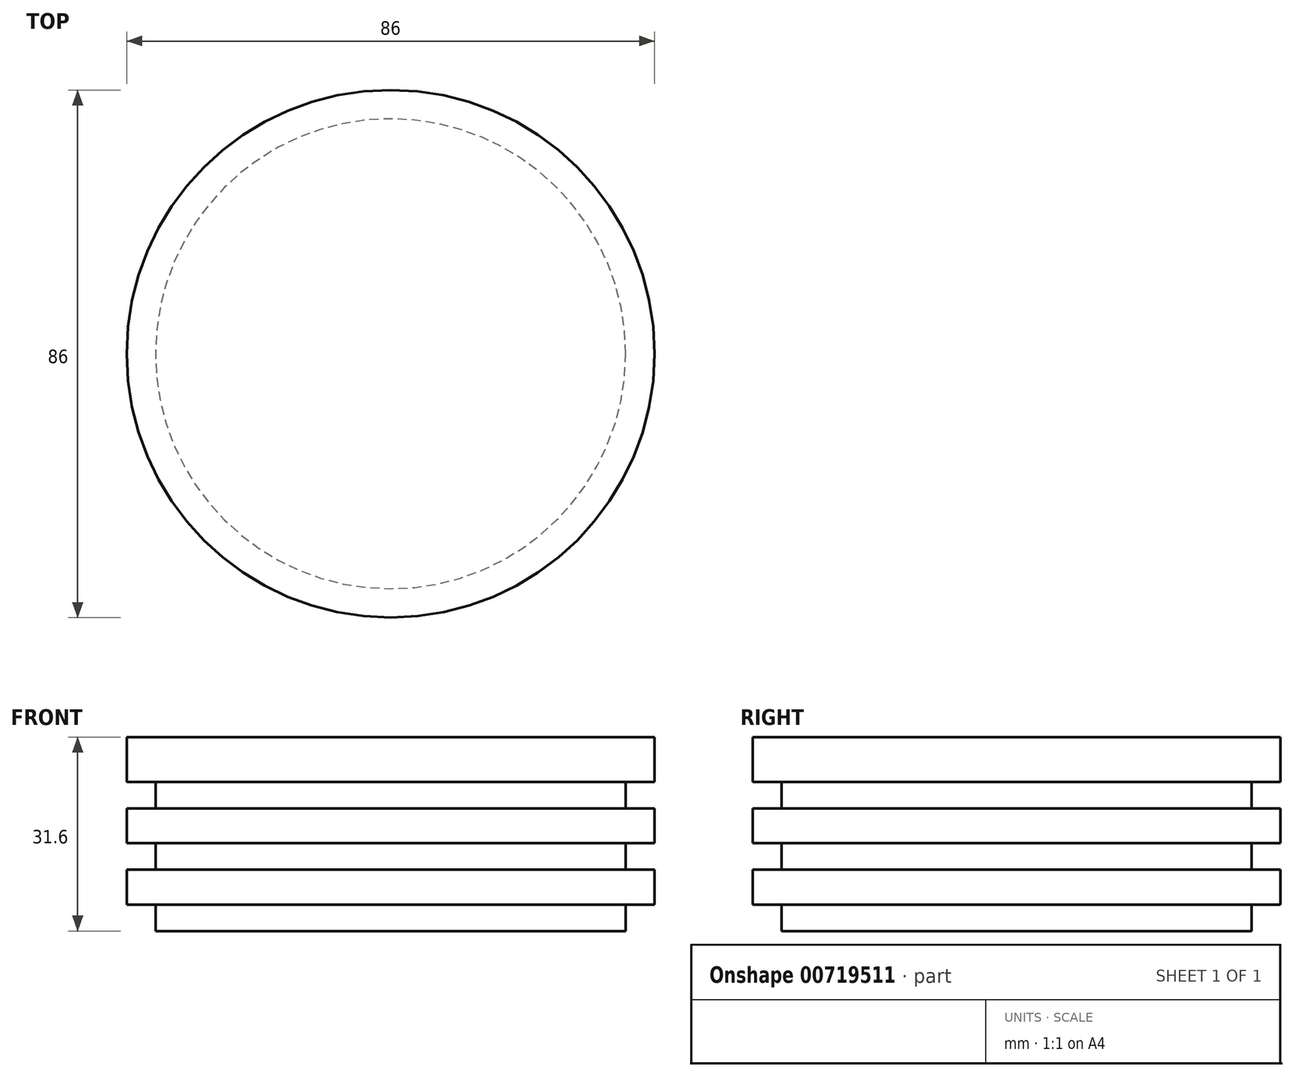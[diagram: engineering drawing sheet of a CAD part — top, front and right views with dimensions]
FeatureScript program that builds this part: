
annotation { "Feature Type Name" : "Feature", "Feature Type Description" : "" }
export const myFeature = defineFeature(function(context is Context, id is Id, definition is map)
    precondition{}
    {
        {
            var Q0;
            Q0=qCreatedBy(makeId("Top.planeOp"),FACE);
            var sketch = newSketch(context, id + "F0", { "sketchPlane" : qUnion([Q0])});
            skCircle(sketch, "E0", {"center": v(0, 0) * mm, "radius": 43 * mm});
            skSolve(sketch);
        }
        {
            var Q0;
            Q0=makeQuery(id+"F0.imprint","IMPRINT",FACE,{"disambiguationData":[TD([[makeQuery(id+"F0.imprint","IMPRINT",EDGE,{"derivedFrom":sQuery(id+"F0.wireOp",EDGE,"E0")}),1.0]])]});
            extrude(context, id + "F1", {"entities" : qUnion([Q0]), "depth" : 7.3 * mm, "offsetDistance" : 25 * mm});
        }
        {
            var Q0;
            Q0=makeQuery(id+"F1.opExtrude","CAP_FACE",FACE,{"disambiguationData":[OSD([sQuery(id+"F0.wireOp",EDGE,"E0")])],"isStart":true});
            var sketch = newSketch(context, id + "F2", { "sketchPlane" : qUnion([Q0])});
            skCircle(sketch, "E1", {"center": v(0, 0) * mm, "radius": 38.3 * mm});
            skSolve(sketch);
        }
        {
            var Q0;
            Q0=makeQuery(id+"F2.imprint","IMPRINT",FACE,{"disambiguationData":[TD([[makeQuery(id+"F2.imprint","IMPRINT",EDGE,{"derivedFrom":sQuery(id+"F2.wireOp",EDGE,"E1")}),1.0]])]});
            extrude(context, id + "F3", {"entities" : qUnion([Q0]), "operationType" : NewBodyOperationType.ADD, "depth" : 4.3 * mm, "offsetDistance" : 25 * mm});
        }
        {
            var Q0;
            Q0=makeQuery(id+"F3.opExtrude","CAP_FACE",FACE,{"disambiguationData":[OSD([sQuery(id+"F2.wireOp",EDGE,"E1")])],"isStart":false});
            var sketch = newSketch(context, id + "F4", { "sketchPlane" : qUnion([Q0])});
            skCircle(sketch, "E2.0", {"center": v(0, 0) * mm, "radius": 43 * mm});
            skSolve(sketch);
        }
        {
            var Q0;
            Q0 = qSketchRegion(id + "F4", true);
            extrude(context, id + "F5", {"entities" : qUnion([Q0]), "operationType" : NewBodyOperationType.ADD, "depth" : 5.7 * mm, "offsetDistance" : 25 * mm});
        }
        {
            var Q0;
            Q0=makeQuery(id+"F5.opExtrude","CAP_FACE",FACE,{"disambiguationData":[OSD([sQuery(id+"F4.wireOp",EDGE,"E2.0")])],"isStart":false});
            var sketch = newSketch(context, id + "F6", { "sketchPlane" : qUnion([Q0])});
            skCircle(sketch, "E3.0", {"center": v(0, 0) * mm, "radius": 38.3 * mm});
            skSolve(sketch);
        }
        {
            var Q0;
            Q0=makeQuery(id+"F6.imprint","IMPRINT",FACE,{"disambiguationData":[TD([[makeQuery(id+"F6.imprint","IMPRINT",EDGE,{"derivedFrom":sQuery(id+"F6.wireOp",EDGE,"E3.0")}),1.0]])]});
            extrude(context, id + "F7", {"entities" : qUnion([Q0]), "operationType" : NewBodyOperationType.ADD, "depth" : 4.3 * mm, "offsetDistance" : 25 * mm});
        }
        {
            var Q0;
            Q0=makeQuery(id+"F7.opExtrude","CAP_FACE",FACE,{"disambiguationData":[OSD([sQuery(id+"F6.wireOp",EDGE,"E3.0")])],"isStart":false});
            var sketch = newSketch(context, id + "F8", { "sketchPlane" : qUnion([Q0])});
            skCircle(sketch, "E4.0", {"center": v(0, 0) * mm, "radius": 43 * mm});
            skSolve(sketch);
        }
        {
            var Q0;
            Q0 = qSketchRegion(id + "F8", true);
            extrude(context, id + "F9", {"entities" : qUnion([Q0]), "operationType" : NewBodyOperationType.ADD, "depth" : 5.7 * mm, "offsetDistance" : 25 * mm});
        }
        {
            var Q0;
            Q0=makeQuery(id+"F9.opExtrude","CAP_FACE",FACE,{"disambiguationData":[OSD([sQuery(id+"F8.wireOp",EDGE,"E4.0")])],"isStart":false});
            var sketch = newSketch(context, id + "F10", { "sketchPlane" : qUnion([Q0])});
            skCircle(sketch, "E5.0", {"center": v(0, 0) * mm, "radius": 38.3 * mm});
            skSolve(sketch);
        }
        {
            var Q0;
            Q0 = qSketchRegion(id + "F10", true);
            extrude(context, id + "F11", {"entities" : qUnion([Q0]), "operationType" : NewBodyOperationType.ADD, "depth" : 4.3 * mm, "offsetDistance" : 25 * mm});
        }
    });
